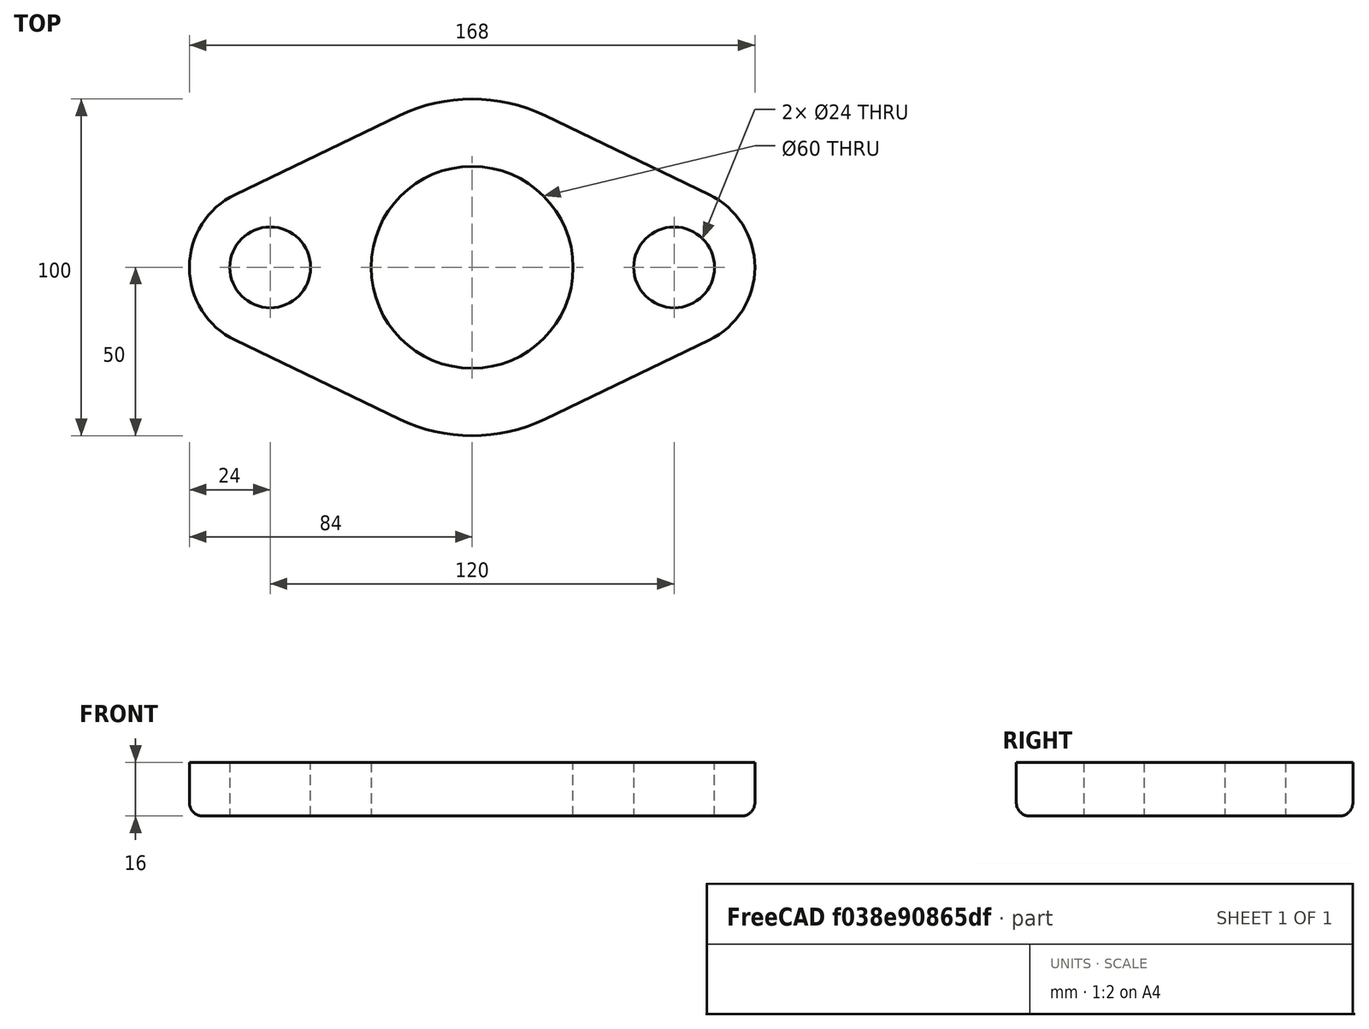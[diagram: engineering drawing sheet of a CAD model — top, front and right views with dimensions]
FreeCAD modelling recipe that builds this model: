
FCSTD DOCUMENT  (FreeCAD 0.20R29410 (Git))
Label: flange-exercise
License: All rights reserved
LicenseURL: http://en.wikipedia.org/wiki/All_rights_reserved
objects: Sketcher::SketchObject×1, PartDesign::Pad×1, PartDesign::Fillet×1, PartDesign::Body×1
note: 6 computed .brp shape members not serialized (recipe doc carries the construction recipe); baked Part::Feature solids carry a one-line shape summary decoded from their .brp

FEATURE [Sketcher::SketchObject] Sketch
  FullyConstrained = true
  MapMode = 5
  Support = -> [XY_Plane]
  sketch-geometry (11):
    g0: Circle CenterX=0 CenterY=0 CenterZ=0 NormalX=0 NormalY=0 NormalZ=1 AngleXU=0 Radius=30
    g1: Circle CenterX=60 CenterY=0 CenterZ=0 NormalX=0 NormalY=0 NormalZ=1 AngleXU=0 Radius=12
    g2: Circle CenterX=-60 CenterY=0 CenterZ=0 NormalX=0 NormalY=0 NormalZ=1 AngleXU=0 Radius=12
    g3: LineSegment StartX=-70.4 StartY=21.6296 StartZ=0 EndX=-21.6667 EndY=45.0617 EndZ=0
    g4: ArcOfCircle CenterX=0 CenterY=0 CenterZ=0 NormalX=0 NormalY=0 NormalZ=1 AngleXU=0 Radius=50 StartAngle=1.12261 EndAngle=2.01898
    g5: LineSegment StartX=21.6667 StartY=45.0617 StartZ=0 EndX=70.4 EndY=21.6296 EndZ=0
    g6: ArcOfCircle CenterX=60 CenterY=0 CenterZ=0 NormalX=0 NormalY=0 NormalZ=1 AngleXU=0 Radius=24 StartAngle=5.16058 EndAngle=7.40579
    g7: LineSegment StartX=70.4 StartY=-21.6296 StartZ=0 EndX=21.6667 EndY=-45.0617 EndZ=0
    g8: ArcOfCircle CenterX=0 CenterY=0 CenterZ=0 NormalX=0 NormalY=0 NormalZ=1 AngleXU=0 Radius=50 StartAngle=4.2642 EndAngle=5.16058
    g9: LineSegment StartX=-21.6667 StartY=-45.0617 StartZ=0 EndX=-70.4 EndY=-21.6296 EndZ=0
    g10: ArcOfCircle CenterX=-60 CenterY=0 CenterZ=0 NormalX=0 NormalY=0 NormalZ=1 AngleXU=0 Radius=24 StartAngle=2.01898 EndAngle=4.2642
  constraints (23):
    c: Coincident(g0,g-1)
    c: Diameter(g0) = 60
    c: PointOnObject(g1,g-1)
    c: Equal(g1,g2)
    c: Diameter(g1) = 24
    c: Symmetric(g2,g1,g-2)
    c: DistanceX(g1) = 60
    c: Tangent(g3,g4) = 1.5708
    c: Tangent(g4,g5) = 1.5708
    c: Tangent(g5,g6) = 1.5708
    c: Tangent(g6,g7) = 1.5708
    c: Tangent(g7,g8) = 1.5708
    c: Tangent(g8,g9) = 1.5708
    c: Tangent(g9,g10) = 1.5708
    c: Tangent(g10,g3) = 1.5708
    c: Coincident(g10,g2)
    c: Coincident(g6,g1)
    c: Equal(g6,g10)
    c: Radius(g6) = 24
    c: Equal(g8,g4)
    c: Radius(g8) = 50
    c: Coincident(g0,g8)
    c: Coincident(g0,g4)
FEATURE [PartDesign::Pad] Pad
  Direction = (0,0,1)
  Length = 16
  Length2 = 10
  Profile = -> Sketch
  ReferenceAxis = -> Sketch [N_Axis]
  Type = 0
FEATURE [PartDesign::Fillet] Fillet
  Base = -> Pad [Edge3]
  BaseFeature = -> Pad
  Radius = 4
  SupportTransform = false
  UseAllEdges = false
FEATURE [PartDesign::Body] Body
  Group = -> [Sketch,Pad,Fillet]
  Origin = -> Origin
  Tip = -> Fillet
